# Revit family: Shower_Receptors-Willoughby-AS
name_source: partatom
category: Plumbing Fixtures
revit_build: Autodesk Revit 2014 (Build: 20130308_1515(x64)
units: mm (PartAtom-declared; Revit-internal decimal feet)

## types (3) — shared parameters
CW Connection = No
Default Elevation = 0' - 0"
Depth = 3' - 0"
HW Connection = No
Height = 0' - 5 1/4"
Manufacturer = Willoughby Industries
Revision = A
URL = www.willoughby-ind.com
Vent Connection = No
Waste Connection = Yes
Waste DIA = 4"

## per-type parameters (varying)
| type | Aquasurf Solid Surface | Description | Drain Distance | Model | Type Comments | Width | Width/2 |
| 36X48 (AS-S3648) | Solid Surface Acrylic Resin-Willoughby | 36x48 Shower Pan | 2' - 0" | AS-S3648 | Rectangular Pan | 4' - 0" | 2' - 0" |
| 36X36 (AS-S3636) | Solid Surface Acrylic Resin-Willoughby(1) | 36x36 Shower Pan | 1' - 6" | AS-S3636 | Square Pan | 3' - 0" | 1' - 6" |
| 36x60 (AS-S3660) | Solid Surface Acrylic Resin-Willoughby | 36x60 Shower Pan | 2' - 6" | AS-S3660 | Rectangular Pan | 5' - 0" | 2' - 6" |

## geometry (parser evidence)
native form markers: Extrusion x3, Sweep x1
no freeform markers — native parametric forms only
